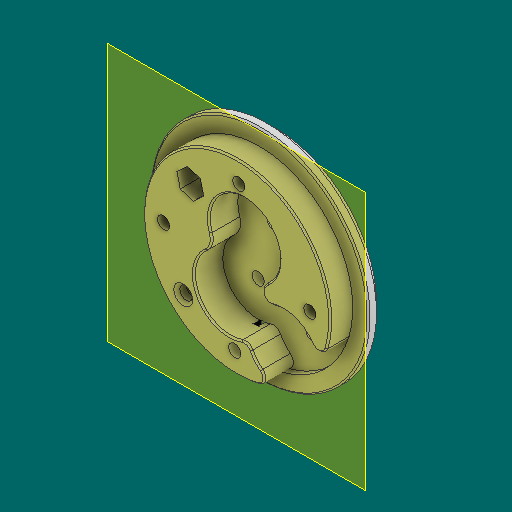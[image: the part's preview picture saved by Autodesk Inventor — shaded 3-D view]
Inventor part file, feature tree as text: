
AUTODESK INVENTOR PART (.ipt)
format: ipt  version: 2023.1 (Build 271208000, 208)  size: 265,728 bytes
history: native  units: in
note: dims shown in document units (in); Inventor stores cm internally (conversion verified against a paired STEP export)
features: sketch x6, other x3, plane x1
ambient origin geometry x8: Origin, YZ Plane, XZ Plane, XY Plane, X Axis, Y Axis, Z Axis, Center Point
bodies: Solid1 (feature_tree)
feature tree (10):
  other  "DiffCap.ipt"
  other  "Solid1::DiffCap.ipt"
  other  "TaggingFeature1"
  sketch  "Sketch1"  dims[d0=0.3937in]
  sketch  "Sketch2"
  sketch  "Sketch3"
  sketch  "Sketch4"
  sketch  "Sketch5"
  sketch  "Sketch6"
  plane  "Work Plane1"
